# Revit family: Mixing_Valve-Thermostatic-Leonard_Valve-High_Capacity-XL_Series
name_source: partatom
category: Pipe Accessories
revit_build: Autodesk Revit 2015 (Build: 20140905_0730(x64)
units: mm (PartAtom-declared; Revit-internal decimal feet)

## types (2) — shared parameters
Date Modified = April 28, 2015
Description = See Part Description
Equipment Abbreviation = MV
Family Version = 1.0
Manufacturer = Leonard Valve Company
Model = See Part Number
Model Disclaimer = For More Information, Contact Leonard Valve Company
Product Documentation Link = http://leonardvalve.industrysuite.com
Product Page URL = http://www.leonardvalve.com
Product data url = https://bimobject.com
URL = http://www.leonardvalve.com
z Beginning of Top Joint Pipe = 1.157 "

## per-type parameters (varying)
| type | z Nested Valve Type | z Total Bottom To Top |
| 150 | XL Valve : XL-150-LF | 32 " |
| 200 | XL Valve : XL-200-SW-LF | 38 " |

note: column(s) folded — value = type name in every type: z Type Model

## geometry (parser evidence)
native form markers: Blend x2, Sweep x7
no freeform markers — native parametric forms only
